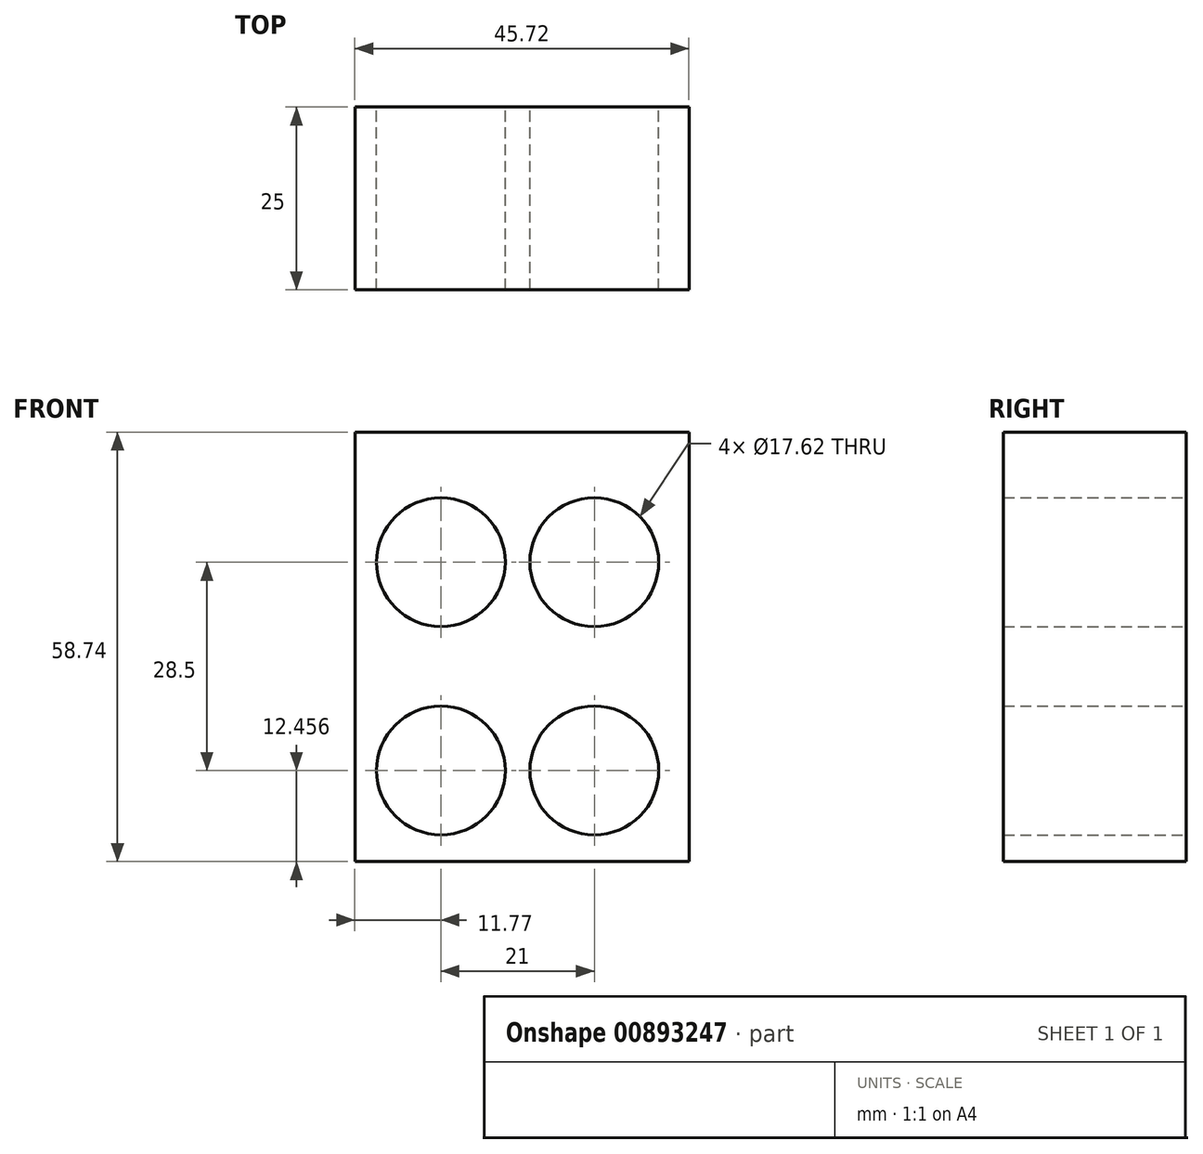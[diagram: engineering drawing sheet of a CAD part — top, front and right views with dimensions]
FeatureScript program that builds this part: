
annotation { "Feature Type Name" : "Feature", "Feature Type Description" : "" }
export const myFeature = defineFeature(function(context is Context, id is Id, definition is map)
    precondition{}
    {
        {
            var Q0;
            Q0=qCreatedBy(makeId("Front.planeOp"),FACE);
            var sketch = newSketch(context, id + "F0", { "sketchPlane" : qUnion([Q0])});
            skLineSegment(sketch, "E0.bottom", {"start": v(-121.7, 32.6) * mm, "end": v(-75.98, 32.6) * mm});
            skLineSegment(sketch, "E0.top", {"start": v(-121.7, -26.13) * mm, "end": v(-75.98, -26.13) * mm});
            skLineSegment(sketch, "E0.left", {"start": v(-121.7, 32.6) * mm, "end": v(-121.7, -26.13) * mm});
            skLineSegment(sketch, "E0.right", {"start": v(-75.98, 32.6) * mm, "end": v(-75.98, -26.13) * mm});
            skCircle(sketch, "E1", {"center": v(-109.93, 14.83) * mm, "radius": 8.8 * mm});
            skCircle(sketch, "E2.0.1.0", {"center": v(-109.93, -13.67) * mm, "radius": 8.8 * mm});
            skCircle(sketch, "E2.1.0.0", {"center": v(-88.93, 14.83) * mm, "radius": 8.8 * mm});
            skCircle(sketch, "E2.1.1.0", {"center": v(-88.93, -13.67) * mm, "radius": 8.8 * mm});
            skLineSegment(sketch, "E2.direction1", {"start": v(-109.93, 14.83) * mm, "end": v(-88.93, 14.83) * mm, "construction": true});
            skLineSegment(sketch, "E2.direction2", {"start": v(-109.93, 14.83) * mm, "end": v(-109.93, -13.67) * mm, "construction": true});
            skSolve(sketch);
        }
        {
            var Q0;
            Q0 = qSketchRegion(id + "F0", true);
            extrude(context, id + "F1", {"entities" : qUnion([Q0]), "depth" : 25 * mm, "offsetDistance" : 25 * mm});
        }
    });
